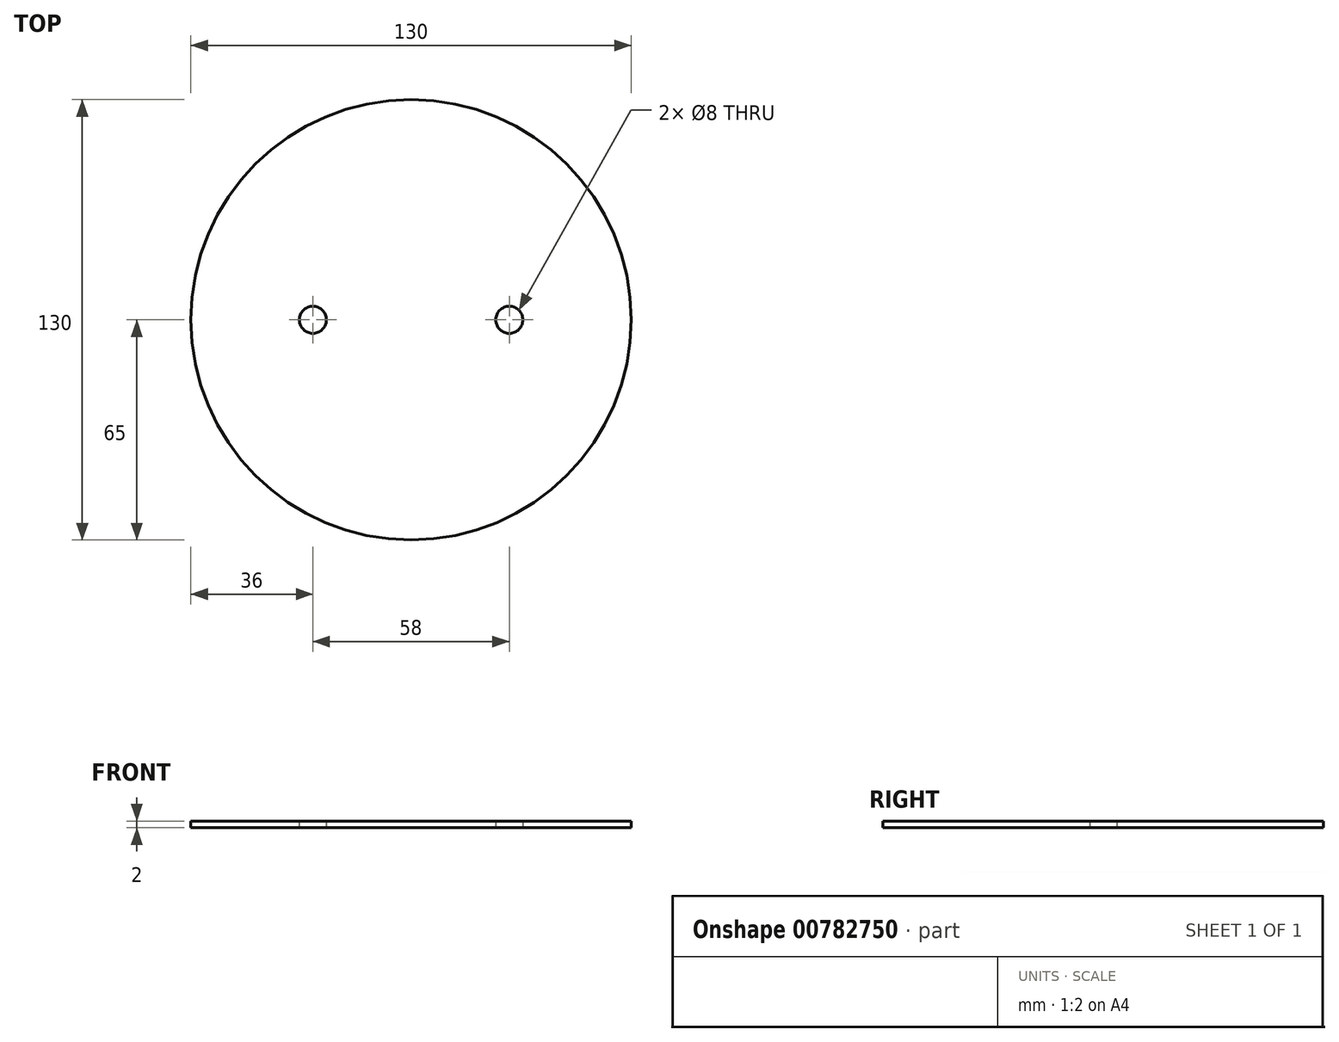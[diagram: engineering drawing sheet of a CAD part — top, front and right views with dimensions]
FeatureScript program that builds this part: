
annotation { "Feature Type Name" : "Feature", "Feature Type Description" : "" }
export const myFeature = defineFeature(function(context is Context, id is Id, definition is map)
    precondition{}
    {
        {
            var Q0;
            Q0=qCreatedBy(makeId("Top.planeOp"),FACE);
            var sketch = newSketch(context, id + "F0", { "sketchPlane" : qUnion([Q0])});
            skCircle(sketch, "E0", {"center": v(0, 0) * mm, "radius": 65 * mm});
            skCircle(sketch, "E1", {"center": v(29, 0) * mm, "radius": 4 * mm});
            skCircle(sketch, "E2", {"center": v(-29, 0) * mm, "radius": 4 * mm});
            skSolve(sketch);
        }
        {
            var Q0;
            Q0 = qSketchRegion(id + "F0", true);
            extrude(context, id + "F1", {"entities" : qUnion([Q0]), "depth" : 2 * mm, "offsetDistance" : 25 * mm});
        }
    });
